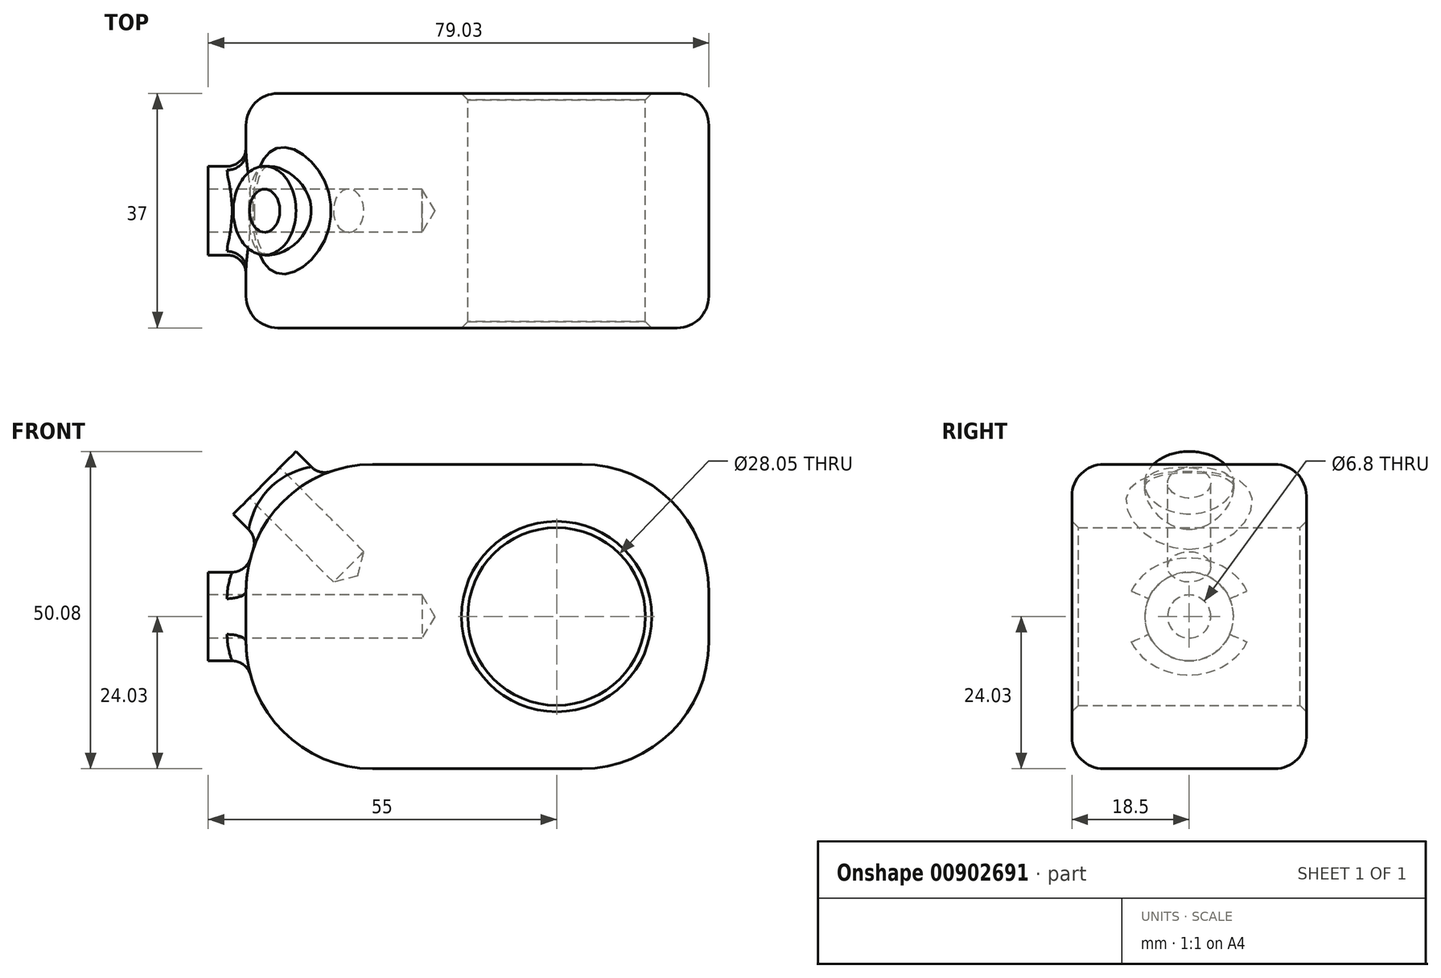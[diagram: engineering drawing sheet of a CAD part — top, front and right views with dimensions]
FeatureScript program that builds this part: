
annotation { "Feature Type Name" : "Feature", "Feature Type Description" : "" }
export const myFeature = defineFeature(function(context is Context, id is Id, definition is map)
    precondition{}
    {
        {
            var Q0;
            Q0=qCreatedBy(makeId("Front.planeOp"),FACE);
            var sketch = newSketch(context, id + "F0", { "sketchPlane" : qUnion([Q0])});
            skCircle(sketch, "E0", {"center": v(0, 0) * mm, "radius": 14.03 * mm});
            skLineSegment(sketch, "E1.bottom", {"start": v(-29.03, -24.03) * mm, "end": v(4.03, -24.03) * mm});
            skLineSegment(sketch, "E1.top", {"start": v(-29.03, 24.02) * mm, "end": v(4.02, 24.02) * mm});
            skLineSegment(sketch, "E1.left", {"start": v(-49.03, -4.03) * mm, "end": v(-49.03, 4.02) * mm});
            skLineSegment(sketch, "E1.right", {"start": v(24.03, -4.02) * mm, "end": v(24.03, 4.03) * mm});
            skLineSegment(sketch, "E2", {"start": v(0, 24.03) * mm, "end": v(0, -24.03) * mm, "construction": true});
            skPoint(sketch, "E3.visualSharp", {"position": v(-49.03, 24.03) * mm});
            skArc(sketch, "E3.filletArc", {"start": v(-29.03, 24.03) * mm, "mid": v(-43.17, 18.17) * mm, "end": v(-49.03, 4.02) * mm});
            skPoint(sketch, "E4.visualSharp", {"position": v(24.02, 24.02) * mm});
            skArc(sketch, "E4.filletArc", {"start": v(24.02, 4.03) * mm, "mid": v(18.17, 18.17) * mm, "end": v(4.03, 24.02) * mm});
            skPoint(sketch, "E5.visualSharp", {"position": v(-49.02, -24.03) * mm});
            skArc(sketch, "E5.filletArc", {"start": v(-49.02, -4.03) * mm, "mid": v(-43.17, -18.17) * mm, "end": v(-29.03, -24.03) * mm});
            skPoint(sketch, "E6.visualSharp", {"position": v(24.03, -24.03) * mm});
            skArc(sketch, "E6.filletArc", {"start": v(4.03, -24.03) * mm, "mid": v(18.17, -18.17) * mm, "end": v(24.03, -4.02) * mm});
            skSolve(sketch);
        }
        {
            var Q0;
            Q0=makeQuery(id+"F0.imprint","IMPRINT",FACE,{"disambiguationData":[TD([[makeQuery(id+"F0.imprint","IMPRINT",EDGE,{"derivedFrom":sQuery(id+"F0.wireOp",EDGE,"E0")}),-1.0]])]});
            extrude(context, id + "F1", {"entities" : qUnion([Q0]), "depth" : 37 / 2 * mm, "offsetDistance" : 25 * mm, "hasSecondDirection" : true, "secondDirectionOppositeDirection" : true, "secondDirectionDepth" : 18.5 * mm});
        }
        {
            var Q0;
            Q0=qCreatedBy(makeId("Right.planeOp"),FACE);
            cPlane(context, id + "F2", {"entities" : qUnion([Q0]), "cplaneType" : CPlaneType.OFFSET, "offset" : 25 * mm, "oppositeDirection" : true, "width" : 150 * mm, "height" : 150 * mm});
        }
        {
            var Q0;
            Q0=qCreatedBy(id+"F2.planeOp",FACE);
            var sketch = newSketch(context, id + "F3", { "sketchPlane" : qUnion([Q0])});
            skCircle(sketch, "E7", {"center": v(0, 0) * mm, "radius": 7 * mm});
            skSolve(sketch);
        }
        {
            var Q0;
            Q0 = qSketchRegion(id + "F3", true);
            extrude(context, id + "F4", {"entities" : qUnion([Q0]), "operationType" : NewBodyOperationType.ADD, "oppositeDirection" : true, "depth" : 30 * mm, "offsetDistance" : 25 * mm});
        }
        {
            var Q0;
            Q0=makeQuery(id+"F4.opExtrude","CAP_FACE",FACE,{"disambiguationData":[OSD([sQuery(id+"F3.wireOp",EDGE,"E7")])],"isStart":false});
            var sketch = newSketch(context, id + "F5", { "sketchPlane" : qUnion([Q0])});
            skPoint(sketch, "E8", {"position": v(0, 0) * mm});
            skSolve(sketch);
        }
        {
            var Q0;
            Q0=sQuery(id+"F5.wireOp",VERTEX,"E8");
            var Q1;
            Q1=makeQuery(id+"F1.opExtrude","SWEPT_BODY",BODY,{"disambiguationData":[OSD([sQuery(id+"F0.wireOp",EDGE,"E0"),sQuery(id+"F0.wireOp",EDGE,"E1.bottom"),sQuery(id+"F0.wireOp",EDGE,"E1.top"),sQuery(id+"F0.wireOp",EDGE,"E1.left"),sQuery(id+"F0.wireOp",EDGE,"E1.right"),sQuery(id+"F0.wireOp",EDGE,"E3.filletArc"),sQuery(id+"F0.wireOp",EDGE,"E4.filletArc"),sQuery(id+"F0.wireOp",EDGE,"E5.filletArc"),sQuery(id+"F0.wireOp",EDGE,"E6.filletArc")])]});
            hole(context, id + "F6", {"style" : HoleStyle.SIMPLE, "endStyle" : HoleEndStyle.BLIND, "standardTappedOrClearance" : lookupTablePath({ "standard" : "ISO", "fit" : "Normal", "engagement" : "75%", "pitch" : "1.25 mm", "size" : "M8", "type" : "Tapped" }), "standardBlindInLast" : lookupTablePath({ "fit" : "Normal", "standard" : "ISO", "engagement" : "75%", "pitch" : "1.25 mm", "size" : "M8", "type" : "Tapped" }), "holeDiameter" : 6.8 * mm, "majorDiameter" : 8 * mm, "showTappedDepth" : true, "holeDepth" : 33.75 * mm, "isTappedThrough" : true, "tappedDepth" : 30 * mm, "tapClearance" : 3, "locations" : qUnion([Q0]), "scope" : qUnion([Q1])});
        }
        {
            var Q0;
            Q0=makeQuery(id+"F1.opExtrude","CAP_EDGE",EDGE,{"disambiguationData":[OSD([sQuery(id+"F0.wireOp",EDGE,"E1.top")])],"isStart":false});
            var Q1;
            Q1=makeQuery(id+"F1.opExtrude","CAP_EDGE",EDGE,{"disambiguationData":[OSD([sQuery(id+"F0.wireOp",EDGE,"E1.top")])],"isStart":true});
            fillet(context, id + "F7", {"entities" : qUnion([Q0, Q1]), "radius" : 5 * mm, "tangentPropagation" : true, "allowEdgeOverflow" : false});
        }
        {
            var Q0;
            Q0=makeQuery(id+"F1.opExtrude","CAP_EDGE",EDGE,{"disambiguationData":[OSD([sQuery(id+"F0.wireOp",EDGE,"E0")])],"isStart":false});
            var Q1;
            Q1=makeQuery(id+"F1.opExtrude","CAP_EDGE",EDGE,{"disambiguationData":[OSD([sQuery(id+"F0.wireOp",EDGE,"E0")])],"isStart":true});
            chamfer(context, id + "F8", {"entities" : qUnion([Q0, Q1]), "width" : 1 * mm, "tangentPropagation" : true});
        }
        {
            var Q0;
            Q0=makeQuery(id+"F1.opExtrude","SWEPT_EDGE",EDGE,{"disambiguationData":[OSD([sQuery(id+"F0.wireOp",EDGE,"E1.top"),sQuery(id+"F0.wireOp",EDGE,"E3.filletArc")])]});
            cPlane(context, id + "F9", {"entities" : qUnion([Q0]), "cplaneType" : CPlaneType.LINE_ANGLE, "offset" : 25 * mm, "angle" : 45 * degree, "oppositeDirection" : true, "width" : 150 * mm, "height" : 150 * mm});
        }
        {
            var Q0;
            Q0=qCreatedBy(id+"F9.planeOp",FACE);
            var sketch = newSketch(context, id + "F10", { "sketchPlane" : qUnion([Q0])});
            skLineSegment(sketch, "E9", {"start": v(0, -3.54) * mm, "end": v(0, -31.82) * mm, "construction": true});
            skCircle(sketch, "E10", {"center": v(0, -17.68) * mm, "radius": 7 * mm});
            skSolve(sketch);
        }
        {
            var Q0;
            Q0 = qSketchRegion(id + "F10", true);
            var Q1;
            Q1=sQuery(id+"F10.wireOp",EDGE,"E10");
            extrude(context, id + "F11", {"entities" : qUnion([Q0]), "operationType" : NewBodyOperationType.ADD, "surfaceEntities" : qUnion([Q1]), "depth" : 10 * mm, "offsetDistance" : 25 * mm});
        }
        {
            var Q0;
            Q0=makeQuery(id+"F11.opExtrude","CAP_FACE",FACE,{"disambiguationData":[OSD([sQuery(id+"F10.wireOp",EDGE,"E10")])],"isStart":false});
            var sketch = newSketch(context, id + "F12", { "sketchPlane" : qUnion([Q0])});
            skPoint(sketch, "E11", {"position": v(0, -17.68) * mm});
            skSolve(sketch);
        }
        {
            var Q0;
            Q0=sQuery(id+"F12.wireOp",VERTEX,"E11");
            var Q1;
            Q1=makeQuery(id+"F1.opExtrude","SWEPT_BODY",BODY,{"disambiguationData":[OSD([sQuery(id+"F0.wireOp",EDGE,"E0"),sQuery(id+"F0.wireOp",EDGE,"E1.bottom"),sQuery(id+"F0.wireOp",EDGE,"E1.top"),sQuery(id+"F0.wireOp",EDGE,"E1.left"),sQuery(id+"F0.wireOp",EDGE,"E1.right"),sQuery(id+"F0.wireOp",EDGE,"E3.filletArc"),sQuery(id+"F0.wireOp",EDGE,"E4.filletArc"),sQuery(id+"F0.wireOp",EDGE,"E5.filletArc"),sQuery(id+"F0.wireOp",EDGE,"E6.filletArc")])]});
            hole(context, id + "F13", {"style" : HoleStyle.SIMPLE, "endStyle" : HoleEndStyle.BLIND, "standardTappedOrClearance" : lookupTablePath({ "standard" : "ISO", "fit" : "Normal", "engagement" : "75%", "pitch" : "1.25 mm", "size" : "M8", "type" : "Tapped" }), "standardBlindInLast" : lookupTablePath({ "fit" : "Normal", "standard" : "ISO", "engagement" : "75%", "pitch" : "1.25 mm", "size" : "M8", "type" : "Tapped" }), "holeDiameter" : 6.8 * mm, "majorDiameter" : 8 * mm, "showTappedDepth" : true, "holeDepth" : 18.75 * mm, "isTappedThrough" : true, "tappedDepth" : 15 * mm, "tapClearance" : 3, "locations" : qUnion([Q0]), "scope" : qUnion([Q1])});
        }
        {
            var Q0;
            Q0=makeQuery(id+"F11.boolean.opBoolean","INTERSECT",EDGE,{"derivedFrom":[makeQuery(id+"F1.opExtrude","SWEPT_FACE",FACE,{"disambiguationData":[OSD([sQuery(id+"F0.wireOp",EDGE,"E3.filletArc")])]}),makeQuery(id+"F11.opExtrude","SWEPT_FACE",FACE,{"disambiguationData":[OSD([sQuery(id+"F10.wireOp",EDGE,"E10")])]})]});
            var Q1;
            Q1=makeQuery(id+"F4.boolean.opBoolean","INTERSECT",EDGE,{"disambiguationData":[OD(1.0)],"derivedFrom":[makeQuery(id+"F1.opExtrude","SWEPT_FACE",FACE,{"disambiguationData":[OSD([sQuery(id+"F0.wireOp",EDGE,"E1.left")])]}),makeQuery(id+"F4.opExtrude","SWEPT_FACE",FACE,{"disambiguationData":[OSD([sQuery(id+"F3.wireOp",EDGE,"E7")])]})]});
            fillet(context, id + "F14", {"entities" : qUnion([Q0, Q1]), "radius" : 3 * mm, "tangentPropagation" : true, "allowEdgeOverflow" : false});
        }
    });
